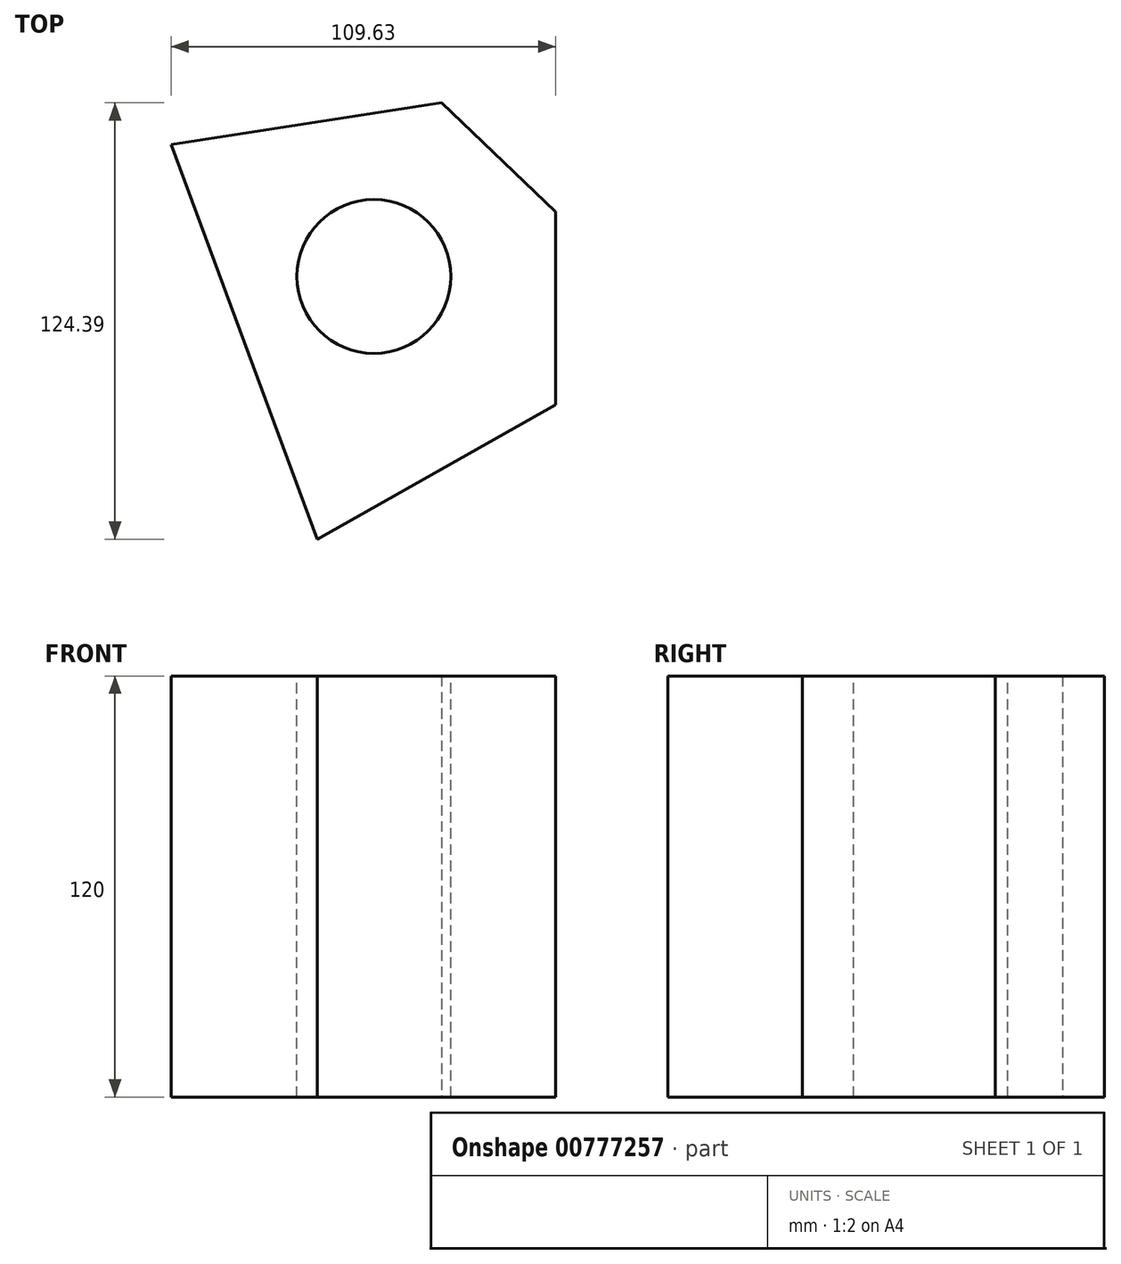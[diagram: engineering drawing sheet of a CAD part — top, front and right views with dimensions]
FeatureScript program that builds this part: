
annotation { "Feature Type Name" : "Feature", "Feature Type Description" : "" }
export const myFeature = defineFeature(function(context is Context, id is Id, definition is map)
    precondition{}
    {
        {
            var Q0;
            Q0=qCreatedBy(makeId("Top.planeOp"),FACE);
            var sketch = newSketch(context, id + "F0", { "sketchPlane" : qUnion([Q0])});
            skLineSegment(sketch, "E0", {"start": v(-57.77, 67.94) * mm, "end": v(19.33, 79.8) * mm});
            skLineSegment(sketch, "E1", {"start": v(19.33, 79.8) * mm, "end": v(51.86, 48.7) * mm});
            skLineSegment(sketch, "E2", {"start": v(51.86, 48.7) * mm, "end": v(51.86, -6.3) * mm});
            skLineSegment(sketch, "E3", {"start": v(51.86, -6.3) * mm, "end": v(-16.1, -44.59) * mm});
            skLineSegment(sketch, "E4", {"start": v(-16.1, -44.59) * mm, "end": v(-57.77, 67.94) * mm});
            skSolve(sketch);
        }
        {
            var Q0;
            Q0=makeQuery(id+"F0.imprint","IMPRINT",FACE,{"disambiguationData":[TD([[makeQuery(id+"F0.imprint","IMPRINT",EDGE,{"derivedFrom":sQuery(id+"F0.wireOp",EDGE,"E0")}),-1.0]])]});
            extrude(context, id + "F1", {"entities" : qUnion([Q0]), "depth" : 120 * mm, "offsetDistance" : 25 * mm});
        }
        {
            var Q0;
            Q0=makeQuery(id+"F1.opExtrude","CAP_FACE",FACE,{"disambiguationData":[OSD([sQuery(id+"F0.wireOp",EDGE,"E0"),sQuery(id+"F0.wireOp",EDGE,"E1"),sQuery(id+"F0.wireOp",EDGE,"E2"),sQuery(id+"F0.wireOp",EDGE,"E3"),sQuery(id+"F0.wireOp",EDGE,"E4")])],"isStart":false});
            var sketch = newSketch(context, id + "F2", { "sketchPlane" : qUnion([Q0])});
            skCircle(sketch, "E5", {"center": v(0, 30.3) * mm, "radius": 21.95 * mm});
            skSolve(sketch);
        }
        {
            var Q0;
            Q0=makeQuery(id+"F2.imprint","IMPRINT",FACE,{"disambiguationData":[TD([[makeQuery(id+"F2.imprint","IMPRINT",EDGE,{"derivedFrom":sQuery(id+"F2.wireOp",EDGE,"E5")}),1.0]])]});
            extrude(context, id + "F3", {"entities" : qUnion([Q0]), "operationType" : NewBodyOperationType.REMOVE, "endBound" : BoundingType.THROUGH_ALL, "oppositeDirection" : true, "depth" : 106.48 * mm, "offsetDistance" : 25 * mm});
        }
    });
